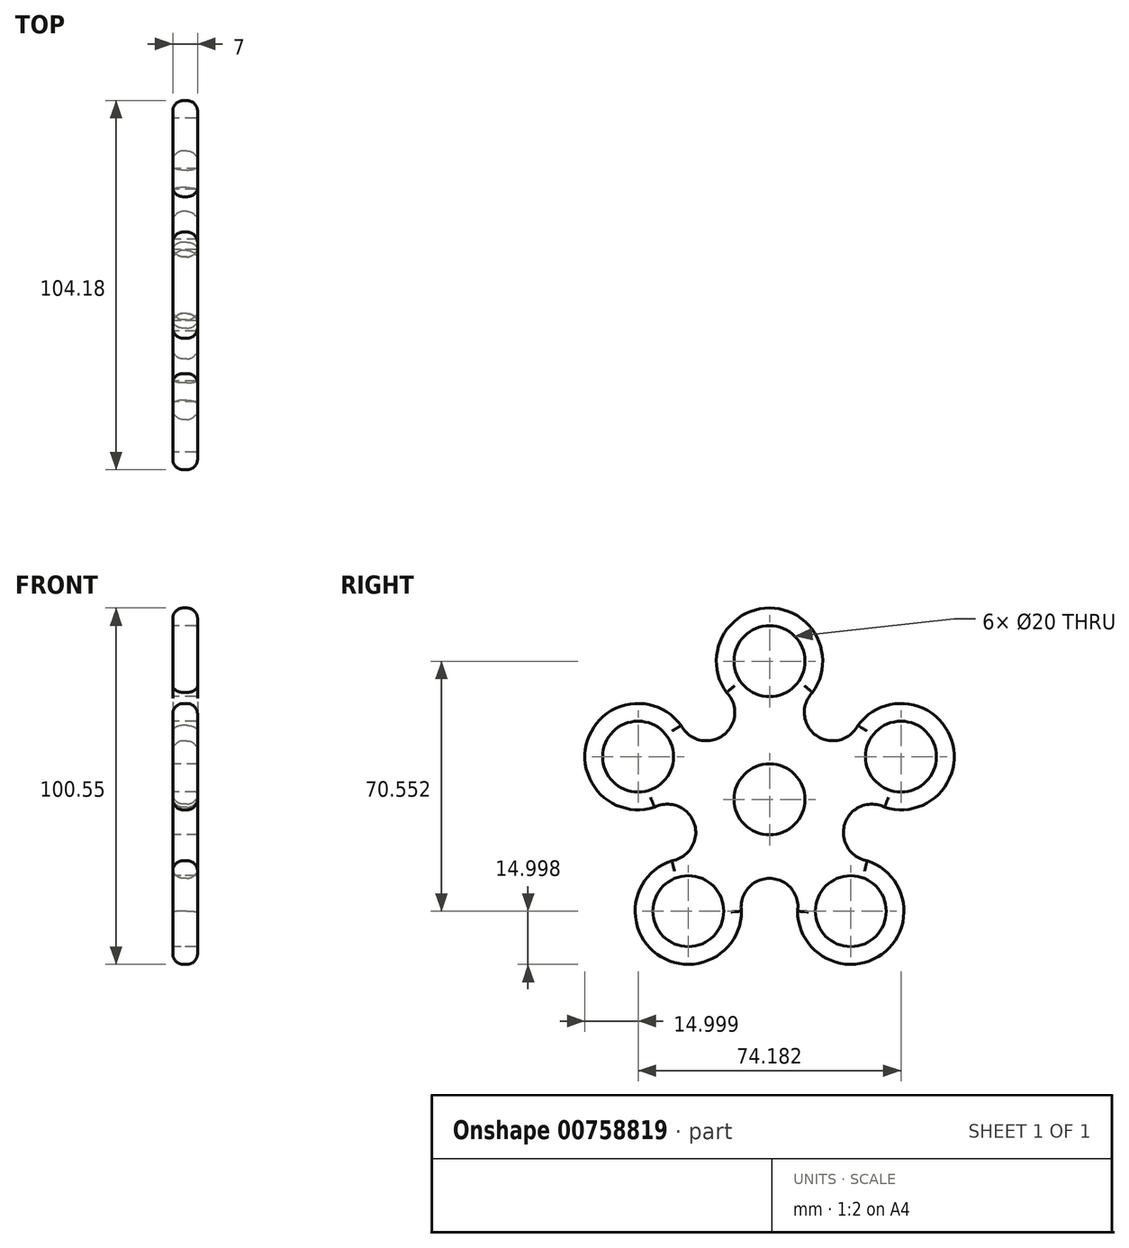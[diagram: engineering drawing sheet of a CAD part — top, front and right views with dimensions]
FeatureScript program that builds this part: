
annotation { "Feature Type Name" : "Feature", "Feature Type Description" : "" }
export const myFeature = defineFeature(function(context is Context, id is Id, definition is map)
    precondition{}
    {
        {
            var Q0;
            Q0=qCreatedBy(makeId("Right.planeOp"),FACE);
            var sketch = newSketch(context, id + "F0", { "sketchPlane" : qUnion([Q0])});
            skLineSegment(sketch, "E0", {"start": v(0, 0) * mm, "end": v(0, 39) * mm});
            skPoint(sketch, "E1.center", {"position": v(0, 0) * mm});
            skCircle(sketch, "E2", {"center": v(0, 39) * mm, "radius": 15 * mm});
            skCircle(sketch, "E3.1.0", {"center": v(-37.1, 12.05) * mm, "radius": 15 * mm});
            skCircle(sketch, "E3.2.0", {"center": v(-22.92, -31.55) * mm, "radius": 15 * mm});
            skCircle(sketch, "E3.3.0", {"center": v(22.92, -31.55) * mm, "radius": 15 * mm});
            skCircle(sketch, "E3.4.0", {"center": v(37.1, 12.05) * mm, "radius": 15 * mm});
            skArc(sketch, "E4", {"start": v(12.14, 30.18) * mm, "mid": v(13.12, 18.05) * mm, "end": v(24.96, 20.87) * mm});
            skArc(sketch, "E5.1.0", {"start": v(-24.96, 20.87) * mm, "mid": v(-13.12, 18.05) * mm, "end": v(-12.14, 30.18) * mm});
            skArc(sketch, "E5.2.0", {"start": v(-27.56, -17.29) * mm, "mid": v(-21.22, -6.9) * mm, "end": v(-32.46, -2.21) * mm});
            skArc(sketch, "E5.3.0", {"start": v(7.92, -31.55) * mm, "mid": v(0, -22.31) * mm, "end": v(-7.92, -31.55) * mm});
            skArc(sketch, "E5.4.0", {"start": v(32.46, -2.21) * mm, "mid": v(21.22, -6.9) * mm, "end": v(27.56, -17.29) * mm});
            skCircle(sketch, "E6", {"center": v(-37.1, 12.05) * mm, "radius": 10 * mm});
            skCircle(sketch, "E7.1.0", {"center": v(-22.92, -31.55) * mm, "radius": 10 * mm});
            skCircle(sketch, "E7.2.0", {"center": v(22.92, -31.55) * mm, "radius": 10 * mm});
            skCircle(sketch, "E7.3.0", {"center": v(37.1, 12.05) * mm, "radius": 10 * mm});
            skCircle(sketch, "E7.4.0", {"center": v(0, 39) * mm, "radius": 10 * mm});
            skSolve(sketch);
        }
        {
            var Q0;
            {var subQ6=sQuery(id+"F0.wireOp",EDGE,"E2");var subQ16=makeQuery(id+"F0.imprint","IMPRINT",VERTEX,{"derivedFrom":subQ6});Q0=makeQuery(id+"F0.imprint","IMPRINT",FACE,{"disambiguationData":[TD([[makeQuery(id+"F0.imprint","IMPRINT",EDGE,{"disambiguationData":[TD([[subQ16,1.0]])],"derivedFrom":subQ6}),-1.0]])]});}
            var Q1;
            Q1=makeQuery(id+"F0.imprint","IMPRINT",FACE,{"disambiguationData":[TD([[makeQuery(id+"F0.imprint","IMPRINT",EDGE,{"derivedFrom":sQuery(id+"F0.wireOp",EDGE,"E7.3.0")}),-1.0]])]});
            var Q2;
            Q2=makeQuery(id+"F0.imprint","IMPRINT",FACE,{"disambiguationData":[TD([[makeQuery(id+"F0.imprint","IMPRINT",EDGE,{"derivedFrom":sQuery(id+"F0.wireOp",EDGE,"E7.2.0")}),-1.0]])]});
            var Q3;
            Q3=makeQuery(id+"F0.imprint","IMPRINT",FACE,{"disambiguationData":[TD([[makeQuery(id+"F0.imprint","IMPRINT",EDGE,{"derivedFrom":sQuery(id+"F0.wireOp",EDGE,"E7.1.0")}),-1.0]])]});
            var Q4;
            Q4=makeQuery(id+"F0.imprint","IMPRINT",FACE,{"disambiguationData":[TD([[makeQuery(id+"F0.imprint","IMPRINT",EDGE,{"derivedFrom":sQuery(id+"F0.wireOp",EDGE,"E6")}),-1.0]])]});
            var Q5;
            Q5=makeQuery(id+"F0.imprint","IMPRINT",FACE,{"disambiguationData":[TD([[makeQuery(id+"F0.imprint","IMPRINT",EDGE,{"derivedFrom":sQuery(id+"F0.wireOp",EDGE,"E7.4.0")}),-1.0]])]});
            extrude(context, id + "F1", {"entities" : qUnion([Q0, Q1, Q2, Q3, Q4, Q5]), "depth" : 7 * mm, "offsetDistance" : 25.4 * mm});
        }
        {
            var Q0;
            Q0=makeQuery(id+"F1.opExtrude","CAP_EDGE",EDGE,{"disambiguationData":[OSD([sQuery(id+"F0.wireOp",EDGE,"E3.1.0")])],"isStart":false});
            var Q1;
            Q1=makeQuery(id+"F1.opExtrude","CAP_EDGE",EDGE,{"disambiguationData":[OSD([sQuery(id+"F0.wireOp",EDGE,"E5.1.0")])],"isStart":false});
            var Q2;
            Q2=makeQuery(id+"F1.opExtrude","CAP_EDGE",EDGE,{"disambiguationData":[OSD([sQuery(id+"F0.wireOp",EDGE,"E2")])],"isStart":false});
            var Q3;
            Q3=makeQuery(id+"F1.opExtrude","CAP_EDGE",EDGE,{"disambiguationData":[OSD([sQuery(id+"F0.wireOp",EDGE,"E4")])],"isStart":false});
            var Q4;
            Q4=makeQuery(id+"F1.opExtrude","CAP_EDGE",EDGE,{"disambiguationData":[OSD([sQuery(id+"F0.wireOp",EDGE,"E3.4.0")])],"isStart":false});
            var Q5;
            Q5=makeQuery(id+"F1.opExtrude","CAP_EDGE",EDGE,{"disambiguationData":[OSD([sQuery(id+"F0.wireOp",EDGE,"E5.4.0")])],"isStart":false});
            var Q6;
            Q6=makeQuery(id+"F1.opExtrude","CAP_EDGE",EDGE,{"disambiguationData":[OSD([sQuery(id+"F0.wireOp",EDGE,"E3.3.0")])],"isStart":false});
            var Q7;
            Q7=makeQuery(id+"F1.opExtrude","CAP_EDGE",EDGE,{"disambiguationData":[OSD([sQuery(id+"F0.wireOp",EDGE,"E5.3.0")])],"isStart":false});
            var Q8;
            Q8=makeQuery(id+"F1.opExtrude","CAP_EDGE",EDGE,{"disambiguationData":[OSD([sQuery(id+"F0.wireOp",EDGE,"E3.2.0")])],"isStart":false});
            var Q9;
            Q9=makeQuery(id+"F1.opExtrude","CAP_EDGE",EDGE,{"disambiguationData":[OSD([sQuery(id+"F0.wireOp",EDGE,"E5.2.0")])],"isStart":false});
            var Q10;
            Q10=makeQuery(id+"F1.opExtrude","CAP_EDGE",EDGE,{"disambiguationData":[OSD([sQuery(id+"F0.wireOp",EDGE,"E3.4.0")])],"isStart":true});
            var Q11;
            Q11=makeQuery(id+"F1.opExtrude","CAP_EDGE",EDGE,{"disambiguationData":[OSD([sQuery(id+"F0.wireOp",EDGE,"E5.4.0")])],"isStart":true});
            var Q12;
            Q12=makeQuery(id+"F1.opExtrude","CAP_EDGE",EDGE,{"disambiguationData":[OSD([sQuery(id+"F0.wireOp",EDGE,"E3.3.0")])],"isStart":true});
            var Q13;
            Q13=makeQuery(id+"F1.opExtrude","CAP_EDGE",EDGE,{"disambiguationData":[OSD([sQuery(id+"F0.wireOp",EDGE,"E5.3.0")])],"isStart":true});
            var Q14;
            Q14=makeQuery(id+"F1.opExtrude","CAP_EDGE",EDGE,{"disambiguationData":[OSD([sQuery(id+"F0.wireOp",EDGE,"E3.2.0")])],"isStart":true});
            var Q15;
            Q15=makeQuery(id+"F1.opExtrude","CAP_EDGE",EDGE,{"disambiguationData":[OSD([sQuery(id+"F0.wireOp",EDGE,"E5.2.0")])],"isStart":true});
            var Q16;
            Q16=makeQuery(id+"F1.opExtrude","CAP_EDGE",EDGE,{"disambiguationData":[OSD([sQuery(id+"F0.wireOp",EDGE,"E3.1.0")])],"isStart":true});
            var Q17;
            Q17=makeQuery(id+"F1.opExtrude","CAP_EDGE",EDGE,{"disambiguationData":[OSD([sQuery(id+"F0.wireOp",EDGE,"E5.1.0")])],"isStart":true});
            var Q18;
            Q18=makeQuery(id+"F1.opExtrude","CAP_EDGE",EDGE,{"disambiguationData":[OSD([sQuery(id+"F0.wireOp",EDGE,"E2")])],"isStart":true});
            var Q19;
            Q19=makeQuery(id+"F1.opExtrude","CAP_EDGE",EDGE,{"disambiguationData":[OSD([sQuery(id+"F0.wireOp",EDGE,"E4")])],"isStart":true});
            fillet(context, id + "F2", {"entities" : qUnion([Q0, Q1, Q2, Q3, Q4, Q5, Q6, Q7, Q8, Q9, Q10, Q11, Q12, Q13, Q14, Q15, Q16, Q17, Q18, Q19]), "radius" : 3 * mm, "tangentPropagation" : true, "allowEdgeOverflow" : false});
        }
        {
            var Q0;
            Q0=qCreatedBy(makeId("Right.planeOp"),FACE);
            var sketch = newSketch(context, id + "F3", { "sketchPlane" : qUnion([Q0])});
            skCircle(sketch, "E8", {"center": v(0, 0) * mm, "radius": 10 * mm});
            skSolve(sketch);
        }
        {
            var Q0;
            Q0=makeQuery(id+"F3.imprint","IMPRINT",FACE,{"disambiguationData":[TD([[makeQuery(id+"F3.imprint","IMPRINT",EDGE,{"derivedFrom":sQuery(id+"F3.wireOp",EDGE,"E8")}),1.0]])]});
            extrude(context, id + "F4", {"entities" : qUnion([Q0]), "operationType" : NewBodyOperationType.REMOVE, "depth" : 7 * mm, "offsetDistance" : 25.4 * mm});
        }
        {
            var Q0;
            Q0=makeQuery(id+"F1.opExtrude","CAP_EDGE",EDGE,{"disambiguationData":[OSD([sQuery(id+"F0.wireOp",EDGE,"E7.4.0")])],"isStart":true});
            var Q1;
            Q1=makeQuery(id+"F4.boolean.opBoolean","COPY",EDGE,{"derivedFrom":makeQuery(id+"F4.opExtrude","CAP_EDGE",EDGE,{"disambiguationData":[OSD([sQuery(id+"F3.wireOp",EDGE,"E8")])],"isStart":true})});
            var Q2;
            Q2=makeQuery(id+"F1.opExtrude","CAP_EDGE",EDGE,{"disambiguationData":[OSD([sQuery(id+"F0.wireOp",EDGE,"E7.3.0")])],"isStart":true});
            var Q3;
            Q3=makeQuery(id+"F1.opExtrude","CAP_EDGE",EDGE,{"disambiguationData":[OSD([sQuery(id+"F0.wireOp",EDGE,"E7.2.0")])],"isStart":true});
            var Q4;
            Q4=makeQuery(id+"F1.opExtrude","CAP_EDGE",EDGE,{"disambiguationData":[OSD([sQuery(id+"F0.wireOp",EDGE,"E7.1.0")])],"isStart":true});
            var Q5;
            Q5=makeQuery(id+"F1.opExtrude","CAP_EDGE",EDGE,{"disambiguationData":[OSD([sQuery(id+"F0.wireOp",EDGE,"E6")])],"isStart":true});
            var Q6;
            Q6=makeQuery(id+"F1.opExtrude","CAP_EDGE",EDGE,{"disambiguationData":[OSD([sQuery(id+"F0.wireOp",EDGE,"E6")])],"isStart":false});
            var Q7;
            Q7=makeQuery(id+"F1.opExtrude","CAP_EDGE",EDGE,{"disambiguationData":[OSD([sQuery(id+"F0.wireOp",EDGE,"E7.4.0")])],"isStart":false});
            var Q8;
            Q8=makeQuery(id+"F1.opExtrude","CAP_EDGE",EDGE,{"disambiguationData":[OSD([sQuery(id+"F0.wireOp",EDGE,"E7.3.0")])],"isStart":false});
            var Q9;
            {var subQ0=sQuery(id+"F0.wireOp",EDGE,"E3.3.0");Q9=makeQuery(id+"F2.opFillet","BLEND_EDGE",EDGE,{"blendedFrom":[makeQuery(id+"F1.opExtrude","CAP_EDGE",EDGE,{"disambiguationData":[OSD([subQ0])],"isStart":false}),makeQuery(id+"F1.opExtrude","CAP_FACE",FACE,{"disambiguationData":[OSD([sQuery(id+"F0.wireOp",EDGE,"E2"),sQuery(id+"F0.wireOp",EDGE,"E3.1.0"),sQuery(id+"F0.wireOp",EDGE,"E3.2.0"),subQ0,sQuery(id+"F0.wireOp",EDGE,"E3.4.0"),sQuery(id+"F0.wireOp",EDGE,"E4"),sQuery(id+"F0.wireOp",EDGE,"E5.1.0"),sQuery(id+"F0.wireOp",EDGE,"E5.2.0"),sQuery(id+"F0.wireOp",EDGE,"E5.3.0"),sQuery(id+"F0.wireOp",EDGE,"E5.4.0"),sQuery(id+"F0.wireOp",EDGE,"E6"),sQuery(id+"F0.wireOp",EDGE,"E7.1.0"),sQuery(id+"F0.wireOp",EDGE,"E7.2.0"),sQuery(id+"F0.wireOp",EDGE,"E7.3.0"),sQuery(id+"F0.wireOp",EDGE,"E7.4.0")])],"isStart":false})],"blendedInto":[makeQuery(id+"F1.opExtrude","CAP_FACE",FACE,{"disambiguationData":[OSD([sQuery(id+"F0.wireOp",EDGE,"E2"),sQuery(id+"F0.wireOp",EDGE,"E3.1.0"),sQuery(id+"F0.wireOp",EDGE,"E3.2.0"),subQ0,sQuery(id+"F0.wireOp",EDGE,"E3.4.0"),sQuery(id+"F0.wireOp",EDGE,"E4"),sQuery(id+"F0.wireOp",EDGE,"E5.1.0"),sQuery(id+"F0.wireOp",EDGE,"E5.2.0"),sQuery(id+"F0.wireOp",EDGE,"E5.3.0"),sQuery(id+"F0.wireOp",EDGE,"E5.4.0"),sQuery(id+"F0.wireOp",EDGE,"E6"),sQuery(id+"F0.wireOp",EDGE,"E7.1.0"),sQuery(id+"F0.wireOp",EDGE,"E7.2.0"),sQuery(id+"F0.wireOp",EDGE,"E7.3.0"),sQuery(id+"F0.wireOp",EDGE,"E7.4.0")])],"isStart":false})]});}
            var Q10;
            Q10=makeQuery(id+"F4.boolean.opBoolean","COPY",EDGE,{"derivedFrom":makeQuery(id+"F4.opExtrude","CAP_EDGE",EDGE,{"disambiguationData":[OSD([sQuery(id+"F3.wireOp",EDGE,"E8")])],"isStart":false})});
            var Q11;
            Q11=makeQuery(id+"F1.opExtrude","CAP_EDGE",EDGE,{"disambiguationData":[OSD([sQuery(id+"F0.wireOp",EDGE,"E7.1.0")])],"isStart":false});
            fillet(context, id + "F5", {"entities" : qUnion([Q0, Q1, Q2, Q3, Q4, Q5, Q6, Q7, Q8, Q9, Q10, Q11]), "radius" : 0.5 * mm, "tangentPropagation" : true, "allowEdgeOverflow" : false});
        }
    });
